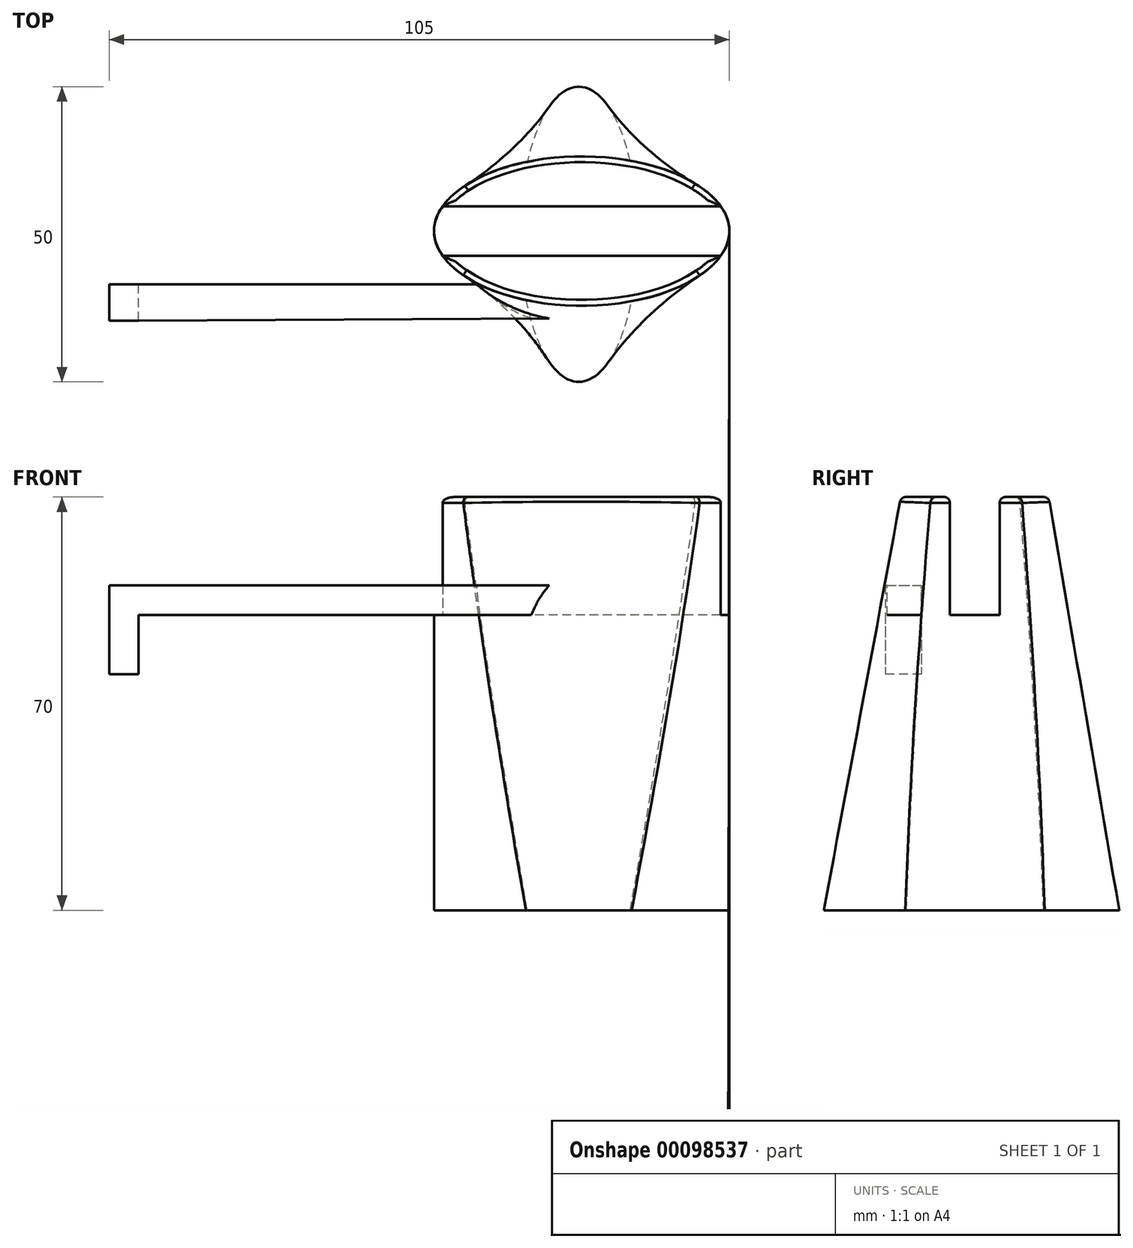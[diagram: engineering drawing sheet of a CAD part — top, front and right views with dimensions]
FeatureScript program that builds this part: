
annotation { "Feature Type Name" : "Feature", "Feature Type Description" : "" }
export const myFeature = defineFeature(function(context is Context, id is Id, definition is map)
    precondition{}
    {
        {
            var Q0;
            Q0=qCreatedBy(makeId("Top.planeOp"),FACE);
            var sketch = newSketch(context, id + "F0", { "sketchPlane" : qUnion([Q0])});
            skEllipse(sketch, "E0", {"center": v(0, 0) * mm, "majorRadius": 25 * mm, "minorRadius": 12.5 * mm, "majorAxis": v(1, 0)});
            skSolve(sketch);
        }
        {
            var Q0;
            Q0=qCreatedBy(makeId("Top.planeOp"),FACE);
            var sketch = newSketch(context, id + "F1", { "sketchPlane" : qUnion([Q0])});
            skEllipse(sketch, "E1", {"center": v(-0.48, -0.55) * mm, "majorRadius": 25 * mm, "minorRadius": 10 * mm, "majorAxis": v(0, 1)});
            skSolve(sketch);
        }
        {
            var Q0;
            Q0=qCreatedBy(makeId("Top.planeOp"),FACE);
            cPlane(context, id + "F2", {"entities" : qUnion([Q0]), "cplaneType" : CPlaneType.OFFSET, "offset" : 70 * mm, "width" : 150 * mm, "height" : 150 * mm});
        }
        {
            var Q0;
            Q0=qCreatedBy(id+"F2.planeOp",FACE);
            var sketch = newSketch(context, id + "F3", { "sketchPlane" : qUnion([Q0])});
            skEllipse(sketch, "E2", {"center": v(0, 0) * mm, "majorRadius": 25 * mm, "minorRadius": 12.5 * mm, "majorAxis": v(1, 0)});
            skSolve(sketch);
        }
        {
            var Q0;
            Q0=makeQuery(id+"F1.imprint","IMPRINT",FACE,{"disambiguationData":[TD([[makeQuery(id+"F1.imprint","IMPRINT",EDGE,{"derivedFrom":sQuery(id+"F1.wireOp",EDGE,"E1")}),1.0]])]});
            var Q1;
            Q1=makeQuery(id+"F3.imprint","IMPRINT",FACE,{"disambiguationData":[TD([[makeQuery(id+"F3.imprint","IMPRINT",EDGE,{"derivedFrom":sQuery(id+"F3.wireOp",EDGE,"E2")}),1.0]])]});
            loft(context, id + "F4", {"sheetProfilesArray" : [{ "sheetProfileEntities" : qUnion([Q0]) }, { "sheetProfileEntities" : qUnion([Q1]) }]});
        }
        {
            var Q1;
            Q1=makeQuery(id+"F0.imprint","IMPRINT",FACE,{"disambiguationData":[TD([[makeQuery(id+"F0.imprint","IMPRINT",EDGE,{"derivedFrom":sQuery(id+"F0.wireOp",EDGE,"E0")}),1.0]])]});
            var Q2;
            Q2=makeQuery(id+"F4.opLoft","CAP_FACE",FACE,{"disambiguationData":[OSD([makeQuery(id+"F3.imprint","IMPRINT",FACE,{"disambiguationData":[TD([[makeQuery(id+"F3.imprint","IMPRINT",EDGE,{"derivedFrom":sQuery(id+"F3.wireOp",EDGE,"E2")}),1.0]])]})])],"isStart":true});
            loft(context, id + "F5", {"operationType" : NewBodyOperationType.ADD, "sheetProfilesArray" : [{ "sheetProfileEntities" : qUnion([Q1]) }, { "sheetProfileEntities" : qUnion([Q2]) }]});
        }
        {
            var Q0;
            Q0=makeQuery(id+"F4.opLoft","CAP_FACE",FACE,{"disambiguationData":[OSD([makeQuery(id+"F3.imprint","IMPRINT",FACE,{"disambiguationData":[TD([[makeQuery(id+"F3.imprint","IMPRINT",EDGE,{"derivedFrom":sQuery(id+"F3.wireOp",EDGE,"E2")}),1.0]])]})])],"isStart":true});
            var sketch = newSketch(context, id + "F6", { "sketchPlane" : qUnion([Q0])});
            skLineSegment(sketch, "E3.bottom", {"start": v(25.13, 4.2) * mm, "end": v(-25.13, 4.2) * mm});
            skLineSegment(sketch, "E3.top", {"start": v(25.13, -4.2) * mm, "end": v(-25.13, -4.2) * mm});
            skLineSegment(sketch, "E3.left", {"start": v(25.13, 4.2) * mm, "end": v(25.13, -4.2) * mm});
            skLineSegment(sketch, "E3.right", {"start": v(-25.13, 4.2) * mm, "end": v(-25.13, -4.2) * mm});
            skPoint(sketch, "E3.middle", {"position": v(0, 0) * mm});
            skSolve(sketch);
        }
        {
            var Q0;
            {var subQ1=sQuery(id+"F3.wireOp",EDGE,"E2");var subQ2=sQuery(id+"F1.wireOp",EDGE,"E1");var subQ3=makeQuery(id+"F5.opLoft","MID_CAP_EDGE",EDGE,{"disambiguationData":[OSD([sQuery(id+"F0.wireOp",EDGE,"E0"),subQ2,subQ1])],"capPos":1.0});var subQ4=makeQuery(id+"F4.opLoft","MID_CAP_EDGE",EDGE,{"disambiguationData":[OSD([subQ2,subQ1])],"capPos":1.0});var subQ8=makeQuery(id+"F5.boolean.opBoolean","MERGE",EDGE,{"disambiguationData":[OD(1.0)],"derivedFrom":[subQ4,subQ3]});var subQ10=sQuery(id+"F6.wireOp",EDGE,"E3.bottom");var subQ12=makeQuery(id+"F6.imprint","INTERSECT",VERTEX,{"derivedFrom":[subQ8,subQ10]});Q0=makeQuery(id+"F6.imprint","IMPRINT",FACE,{"disambiguationData":[TD([[makeQuery(id+"F6.imprint","IMPRINT",EDGE,{"disambiguationData":[TD([[subQ12,-1.0]])],"derivedFrom":subQ10}),1.0]])]});}
            extrude(context, id + "F7", {"entities" : qUnion([Q0]), "operationType" : NewBodyOperationType.REMOVE, "oppositeDirection" : true, "depth" : 20 * mm});
        }
        {
            var Q0;
            {var subQ0=sQuery(id+"F3.wireOp",EDGE,"E2");Q0=makeQuery(id+"F7.boolean.opBoolean","SPLIT",FACE,{"disambiguationData":[TD([makeQuery(id+"F7.opExtrude","SWEPT_FACE",FACE,{"disambiguationData":[OSD([sQuery(id+"F6.wireOp",EDGE,"E3.bottom")])]})])],"derivedFrom":makeQuery(id+"F4.opLoft","CAP_FACE",FACE,{"disambiguationData":[OSD([makeQuery(id+"F3.imprint","IMPRINT",FACE,{"disambiguationData":[TD([[makeQuery(id+"F3.imprint","IMPRINT",EDGE,{"derivedFrom":subQ0}),1.0]])]})])],"isStart":true})});}
            var Q1;
            {var subQ0=sQuery(id+"F3.wireOp",EDGE,"E2");Q1=makeQuery(id+"F7.boolean.opBoolean","SPLIT",FACE,{"disambiguationData":[TD([makeQuery(id+"F7.opExtrude","SWEPT_FACE",FACE,{"disambiguationData":[OSD([sQuery(id+"F6.wireOp",EDGE,"E3.top")])]})])],"derivedFrom":makeQuery(id+"F4.opLoft","CAP_FACE",FACE,{"disambiguationData":[OSD([makeQuery(id+"F3.imprint","IMPRINT",FACE,{"disambiguationData":[TD([[makeQuery(id+"F3.imprint","IMPRINT",EDGE,{"derivedFrom":subQ0}),1.0]])]})])],"isStart":true})});}
            fillet(context, id + "F8", {"entities" : qUnion([Q0, Q1]), "radius" : 1 * mm, "tangentPropagation" : true, "allowEdgeOverflow" : false});
        }
        {
            var Q0;
            Q0=makeQuery(id+"F7.boolean.opBoolean","COPY",FACE,{"derivedFrom":makeQuery(id+"F7.opExtrude","CAP_FACE",FACE,{"disambiguationData":[OSD([sQuery(id+"F0.wireOp",EDGE,"E0"),sQuery(id+"F1.wireOp",EDGE,"E1"),sQuery(id+"F3.wireOp",EDGE,"E2"),sQuery(id+"F6.wireOp",EDGE,"E3.bottom"),sQuery(id+"F6.wireOp",EDGE,"E3.top")])],"isStart":false})});
            cPlane(context, id + "F9", {"entities" : qUnion([Q0]), "cplaneType" : CPlaneType.OFFSET, "offset" : 0 * mm, "width" : 150 * mm, "height" : 150 * mm});
        }
        {
            var Q0;
            Q0=qCreatedBy(id+"F9.planeOp",FACE);
            var sketch = newSketch(context, id + "F10", { "sketchPlane" : qUnion([Q0])});
            skLineSegment(sketch, "E4.bottom", {"start": v(0, -14.77) * mm, "end": v(-75, -15.18) * mm});
            skLineSegment(sketch, "E4.top", {"start": v(0, -9.03) * mm, "end": v(-75, -9.03) * mm});
            skLineSegment(sketch, "E4.left", {"start": v(0, -14.77) * mm, "end": v(0, -9.03) * mm});
            skLineSegment(sketch, "E4.right", {"start": v(-75, -15.18) * mm, "end": v(-75, -9.03) * mm});
            skSolve(sketch);
        }
        {
            var Q0;
            Q0=makeQuery(id+"F10.imprint","IMPRINT",FACE,{"disambiguationData":[TD([[makeQuery(id+"F10.imprint","IMPRINT",EDGE,{"derivedFrom":sQuery(id+"F10.wireOp",EDGE,"E4.top")}),1.0]])]});
            extrude(context, id + "F11", {"entities" : qUnion([Q0]), "operationType" : NewBodyOperationType.ADD, "depth" : 5 * mm});
        }
        {
            var Q0;
            Q0=makeQuery(id+"F11.opExtrude","SWEPT_FACE",FACE,{"disambiguationData":[OSD([sQuery(id+"F10.wireOp",EDGE,"E4.right")])]});
            var sketch = newSketch(context, id + "F12", { "sketchPlane" : qUnion([Q0])});
            skLineSegment(sketch, "E5.bottom", {"start": v(9.03, 55) * mm, "end": v(15.18, 55) * mm});
            skLineSegment(sketch, "E5.top", {"start": v(9.03, 40) * mm, "end": v(15.18, 40) * mm});
            skLineSegment(sketch, "E5.left", {"start": v(9.03, 55) * mm, "end": v(9.03, 40) * mm});
            skLineSegment(sketch, "E5.right", {"start": v(15.18, 55) * mm, "end": v(15.18, 40) * mm});
            skSolve(sketch);
        }
        {
            var Q0;
            Q0=qSketchRegion(id+"F12",true);
            extrude(context, id + "F13", {"entities" : qUnion([Q0]), "operationType" : NewBodyOperationType.ADD, "depth" : 5 * mm});
        }
    });
